# Revit family: S-tank_Solar_SS-HP
name_source: partatom
category: Оборудование
units: mm (PartAtom-declared; Revit-internal decimal feet)

## family parameters
Всегда вертикально = Да
Классификация = Нет
На основе рабочей плоскости = Нет
Общий = Нет
При загрузке вырезать с полостями = Нет
Размер круглого соединителя = Использовать диаметр
Тип детали = Нормальный
Точка расчета площади = Нет

## types (7) — shared parameters
ADSK_URL документации изделия = http://s-tank.ru
ADSK_Группирование = Оборудование
ADSK_Единица измерения = шт.
ADSK_Завод-изготовитель = ООО “С-ТЭНК ВОТЕР ХИТЕРС”
ADSK_Наименование = Бойлер косвенного нагрева
DN1 = 25 мм
DN2 = 15 мм
shrf = 18 мм
Разработка семейств = https://rubim.tech

## per-type parameters (varying)
| type | A | ADSK_Код изделия | ADSK_Марка | ADSK_Масса | B | C | D | E | H | I | J | a | Диаметрсизоляцией |
| SSHP 300 | 125 мм | 2.2001 | SS HP 300 | 73 | 280 мм | 440 мм | 1040 мм | 1200 мм | 1600 мм | 1360 мм | 1030 мм | 105 мм | 630 мм |
| SSHP 500 | 122 мм | 2.2002 | SS HP 500 | 97 | 275 мм | 435 мм | 1035 мм | 1195 мм | 1680 мм | 1355 мм | 1370 мм | 130 мм | 780 мм |
| SSHP 750 | 117 мм | 2.2003 | SS HP 750 | 119 | 265 мм | 425 мм | 1025 мм | 1185 мм | 1630 мм | 1345 мм | 1365 мм | 153 мм | 920 мм |
| SSHP 1000 | 117 мм | 2.2004 | SS HP 1000 | 153 | 265 мм | 510 мм | 1430 мм | 1675 мм | 2205 мм | 1920 мм | 1585 мм | 153 мм | 920 мм |
| SSHP 1200 | 177 мм | 2.2005 | SS HP 1200 | 195 | 315 мм | 505 мм | 1285 мм | 1475 мм | 2080 мм | 1665 мм | 1920 мм | 178 мм | 1070 мм |
| SSHP 1500 | 177 мм | 2.2006 | SS HP 1500 | 225 | 315 мм | 555 мм | 1535 мм | 1775 мм | 2370 мм | 2015 мм | 1655 мм | 178 мм | 1070 мм |
| SSHP 2000 | 250 мм | 2.0007 | SS HP 2000 | 270 | 400 мм | 590 мм | 1370 мм | 1560 мм | 2100 мм | 1750 мм | 2005 мм | 225 мм | 1350 мм |

note: column(s) folded — value = type name in every type: ADSK_Обозначение
